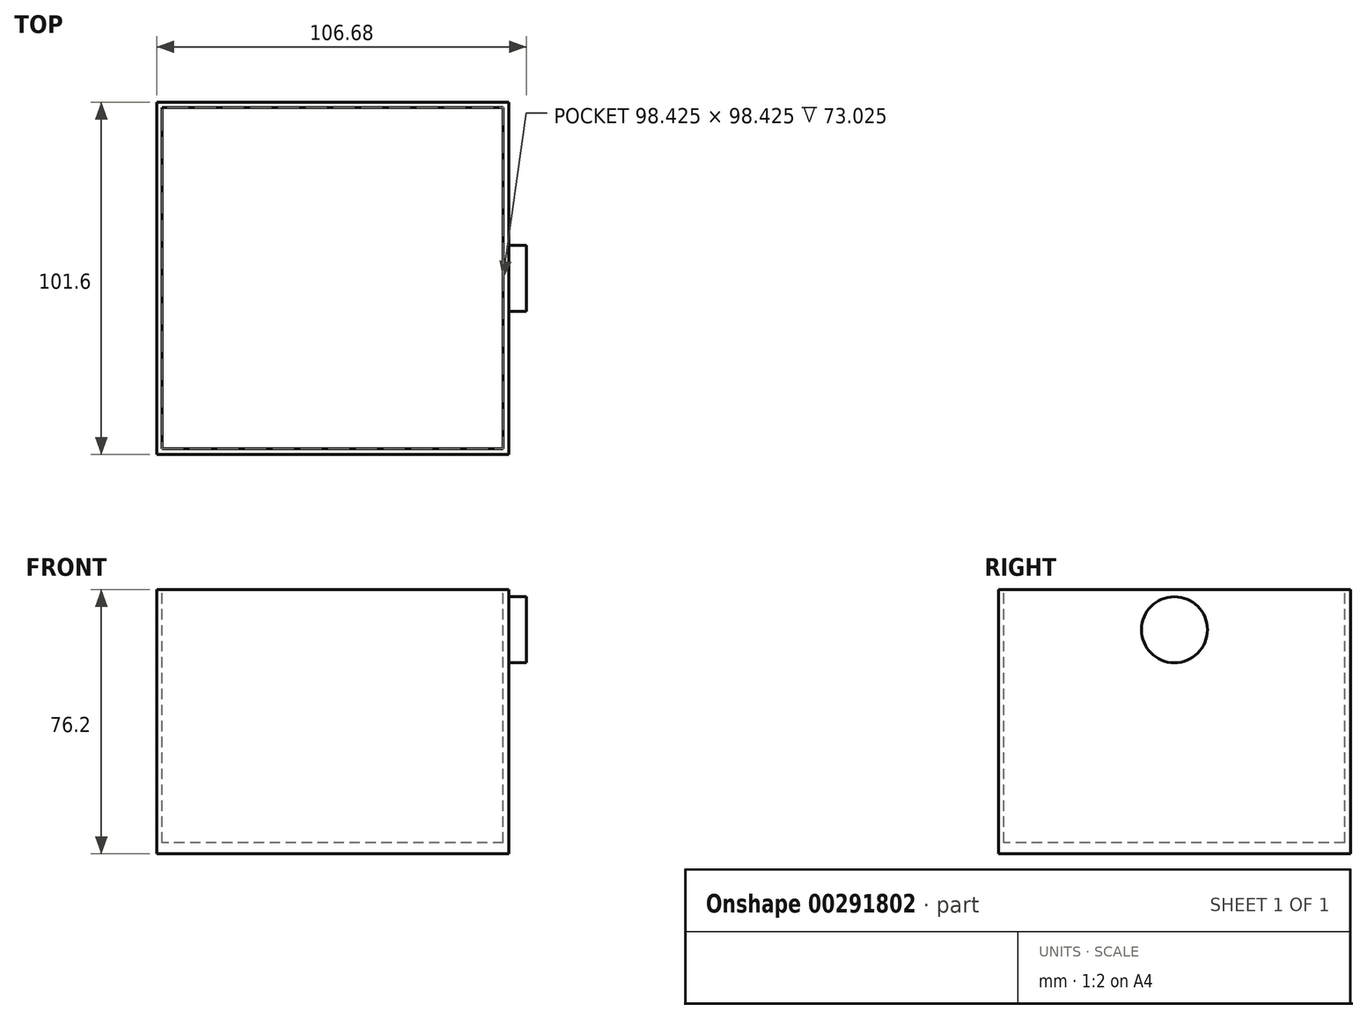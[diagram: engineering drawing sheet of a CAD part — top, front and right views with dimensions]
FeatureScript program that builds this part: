
annotation { "Feature Type Name" : "Feature", "Feature Type Description" : "" }
export const myFeature = defineFeature(function(context is Context, id is Id, definition is map)
    precondition{}
    {
        {
            var Q0;
            Q0=qCreatedBy(makeId("Front.planeOp"),FACE);
            var sketch = newSketch(context, id + "F0", { "sketchPlane" : qUnion([Q0])});
            skLineSegment(sketch, "E0.bottom", {"start": v(50.8, 38.1) * mm, "end": v(-50.8, 38.1) * mm});
            skLineSegment(sketch, "E0.top", {"start": v(50.8, -38.1) * mm, "end": v(-50.8, -38.1) * mm});
            skLineSegment(sketch, "E0.left", {"start": v(50.8, 38.1) * mm, "end": v(50.8, -38.1) * mm});
            skLineSegment(sketch, "E0.right", {"start": v(-50.8, 38.1) * mm, "end": v(-50.8, -38.1) * mm});
            skPoint(sketch, "E0.middle", {"position": v(0, 0) * mm});
            skSolve(sketch);
        }
        {
            var Q0;
            Q0 = qSketchRegion(id + "F0", true);
            extrude(context, id + "F1", {"entities" : qUnion([Q0]), "endBound" : BoundingType.SYMMETRIC, "depth" : 101.6 * mm});
        }
        {
            var Q0;
            Q0=makeQuery(id+"F1.opExtrude","SWEPT_FACE",FACE,{"disambiguationData":[OSD([sQuery(id+"F0.wireOp",EDGE,"E0.bottom")])]});
            var sketch = newSketch(context, id + "F2", { "sketchPlane" : qUnion([Q0])});
            skLineSegment(sketch, "E1.bottom", {"start": v(49.21, 49.21) * mm, "end": v(-49.21, 49.21) * mm});
            skLineSegment(sketch, "E1.top", {"start": v(49.21, -49.21) * mm, "end": v(-49.21, -49.21) * mm});
            skLineSegment(sketch, "E1.left", {"start": v(49.21, 49.21) * mm, "end": v(49.21, -49.21) * mm});
            skLineSegment(sketch, "E1.right", {"start": v(-49.21, 49.21) * mm, "end": v(-49.21, -49.21) * mm});
            skPoint(sketch, "E1.middle", {"position": v(0, 0) * mm});
            skSolve(sketch);
        }
        {
            var Q0;
            Q0 = qSketchRegion(id + "F2", true);
            extrude(context, id + "F3", {"entities" : qUnion([Q0]), "operationType" : NewBodyOperationType.REMOVE, "oppositeDirection" : true, "depth" : 73.02 * mm});
        }
        {
            var Q0;
            Q0=makeQuery(id+"F1.opExtrude","SWEPT_FACE",FACE,{"disambiguationData":[OSD([sQuery(id+"F0.wireOp",EDGE,"E0.left")])]});
            var sketch = newSketch(context, id + "F4", { "sketchPlane" : qUnion([Q0])});
            skCircle(sketch, "E2", {"center": v(0, 26.53) * mm, "radius": 9.53 * mm});
            skSolve(sketch);
        }
        {
            var Q0;
            Q0 = qSketchRegion(id + "F4", true);
            extrude(context, id + "F5", {"entities" : qUnion([Q0]), "operationType" : NewBodyOperationType.ADD, "depth" : 5.08 * mm});
        }
    });
